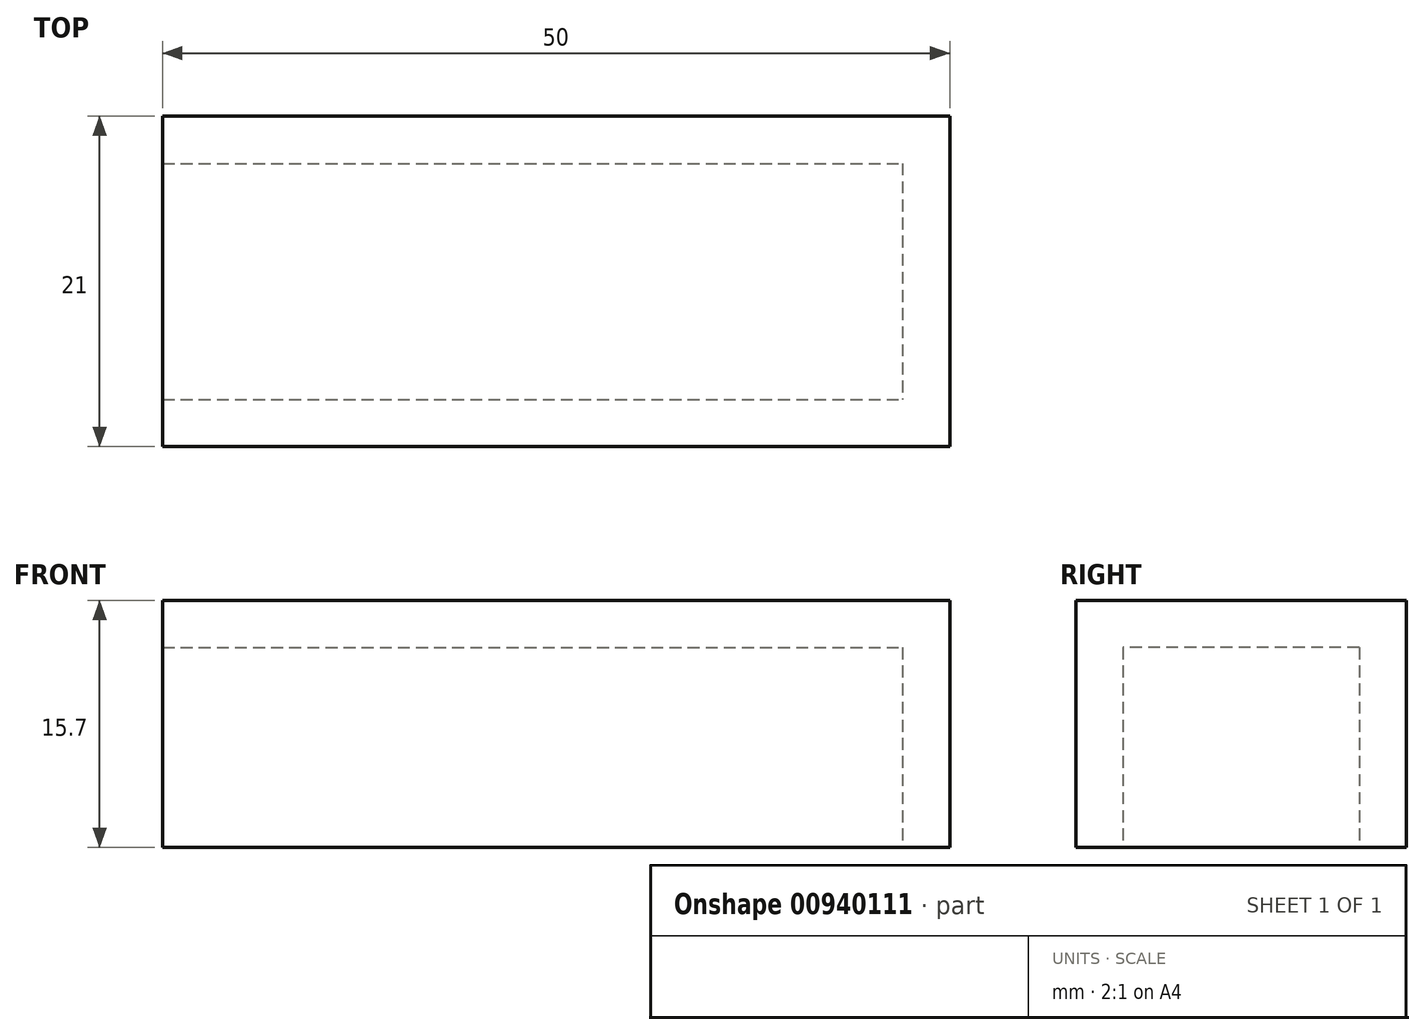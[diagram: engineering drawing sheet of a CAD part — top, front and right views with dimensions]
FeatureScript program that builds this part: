
annotation { "Feature Type Name" : "Feature", "Feature Type Description" : "" }
export const myFeature = defineFeature(function(context is Context, id is Id, definition is map)
    precondition{}
    {
        {
            var Q0;
            Q0=qCreatedBy(makeId("Top.planeOp"),FACE);
            var sketch = newSketch(context, id + "F0", { "sketchPlane" : qUnion([Q0])});
            skLineSegment(sketch, "E0.bottom", {"start": v(0, 0) * mm, "end": v(50, 0) * mm});
            skLineSegment(sketch, "E0.top", {"start": v(0, 21) * mm, "end": v(50, 21) * mm});
            skLineSegment(sketch, "E0.right", {"start": v(50, 0) * mm, "end": v(50, 21) * mm});
            skLineSegment(sketch, "E1.bottom", {"start": v(0, 18) * mm, "end": v(47, 18) * mm});
            skLineSegment(sketch, "E1.top", {"start": v(0, 3) * mm, "end": v(47, 3) * mm});
            skLineSegment(sketch, "E1.right", {"start": v(47, 18) * mm, "end": v(47, 3) * mm});
            skLineSegment(sketch, "E2", {"start": v(0, 21) * mm, "end": v(0, 18) * mm});
            skLineSegment(sketch, "E3", {"start": v(0, 3) * mm, "end": v(0, 0) * mm});
            skSolve(sketch);
        }
        {
            var Q0;
            Q0 = qSketchRegion(id + "F0", true);
            extrude(context, id + "F1", {"entities" : qUnion([Q0]), "depth" : 12.7 * mm, "offsetDistance" : 25.4 * mm});
        }
        {
            var Q0;
            Q0=makeQuery(id+"F1.opExtrude","CAP_FACE",FACE,{"disambiguationData":[OSD([sQuery(id+"F0.wireOp",EDGE,"E0.bottom"),sQuery(id+"F0.wireOp",EDGE,"E0.top"),sQuery(id+"F0.wireOp",EDGE,"E0.left"),sQuery(id+"F0.wireOp",EDGE,"E0.right"),sQuery(id+"F0.wireOp",EDGE,"E1.bottom"),sQuery(id+"F0.wireOp",EDGE,"E1.top"),sQuery(id+"F0.wireOp",EDGE,"E1.left"),sQuery(id+"F0.wireOp",EDGE,"E1.right")])],"isStart":false});
            var sketch = newSketch(context, id + "F2", { "sketchPlane" : qUnion([Q0])});
            skLineSegment(sketch, "E4.bottom", {"start": v(0, 21) * mm, "end": v(50, 21) * mm});
            skLineSegment(sketch, "E4.top", {"start": v(0, 0) * mm, "end": v(50, 0) * mm});
            skLineSegment(sketch, "E4.left", {"start": v(0, 21) * mm, "end": v(0, 0) * mm});
            skLineSegment(sketch, "E4.right", {"start": v(50, 21) * mm, "end": v(50, 0) * mm});
            skSolve(sketch);
        }
        {
            var Q0;
            Q0 = qSketchRegion(id + "F2", true);
            var Q1;
            Q1=makeQuery(id+"F2.imprint","IMPRINT",FACE,{"disambiguationData":[TD([[makeQuery(id+"F2.imprint","IMPRINT",EDGE,{"derivedFrom":makeQuery(id+"F1.opExtrude","CAP_EDGE",EDGE,{"disambiguationData":[OSD([sQuery(id+"F0.wireOp",EDGE,"E1.bottom")])],"isStart":false})}),-1.0]])]});
            extrude(context, id + "F3", {"entities" : qUnion([Q0, Q1]), "operationType" : NewBodyOperationType.ADD, "depth" : 3 * mm, "offsetDistance" : 25.4 * mm});
        }
    });
